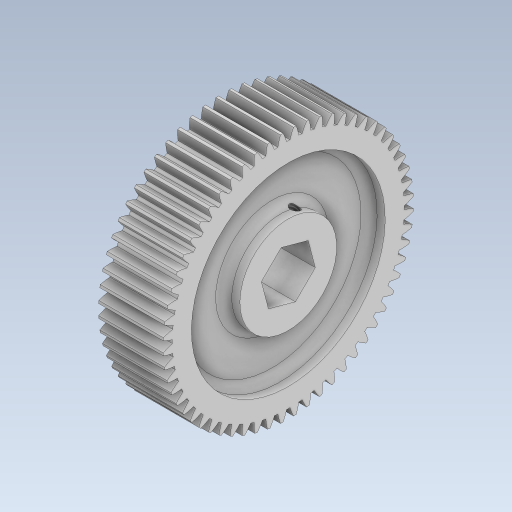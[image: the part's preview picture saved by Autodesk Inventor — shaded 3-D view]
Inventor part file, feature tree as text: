
AUTODESK INVENTOR PART (.ipt)
format: ipt  version: 2023 (Build 270158000, 158)  size: 589,312 bytes
history: native  units: in
note: dims shown in document units (in); Inventor stores cm internally (conversion verified against a paired STEP export)
features: sketch x5, extrude x3, plane x3, fillet x1, hole x1, mirror x1, other x1
ambient origin geometry x8: Origin, YZ Plane, XZ Plane, XY Plane, X Axis, Y Axis, Z Axis, Center Point
bodies: Solid1 (feature_tree)
feature tree (15):
  extrude  "Extrusion1"  TaperAngle=0.0deg  [1 undecoded]
  extrude  "Extrusion2"  Depth=0.375in
  extrude  "Extrusion3"  Depth=0.125in
  fillet  "Fillet1"  Radius=0.125in
  plane  "Work Plane1"
  plane  "Work Plane2"
  sketch  "Sketch4"  dims[d11=0.0625in d12=-0.25in]
  plane  "Work Plane3"
  hole  "Hole1"  [1 undecoded]
  mirror  "Mirror2"
  sketch  "Sketch1"  dims[d0=0.5in d1=0.0in d2=0.0in]
  sketch  "Sketch2"  dims[d4=0.0in d5=0.0in d6=0.375in]
  sketch  "Sketch3"  dims[d7=0.75in d8=1.5in d9=0.125in d10=0.0in]
  sketch  "Sketch5"  dims[d13=-0.1875in d14=15.0deg d15=0.0625in d16=0.0764in d17=0.198in d18=0.435in d19=0.15in d20=0.563in d21=1.0in d22=0.8108in]
  other  "TeethCuts"
note: 2 required parameter values undecoded (feature->parameter linkage not recoverable at this tier; creation-order binding heuristic only, values carry confidence <= 0.55)
